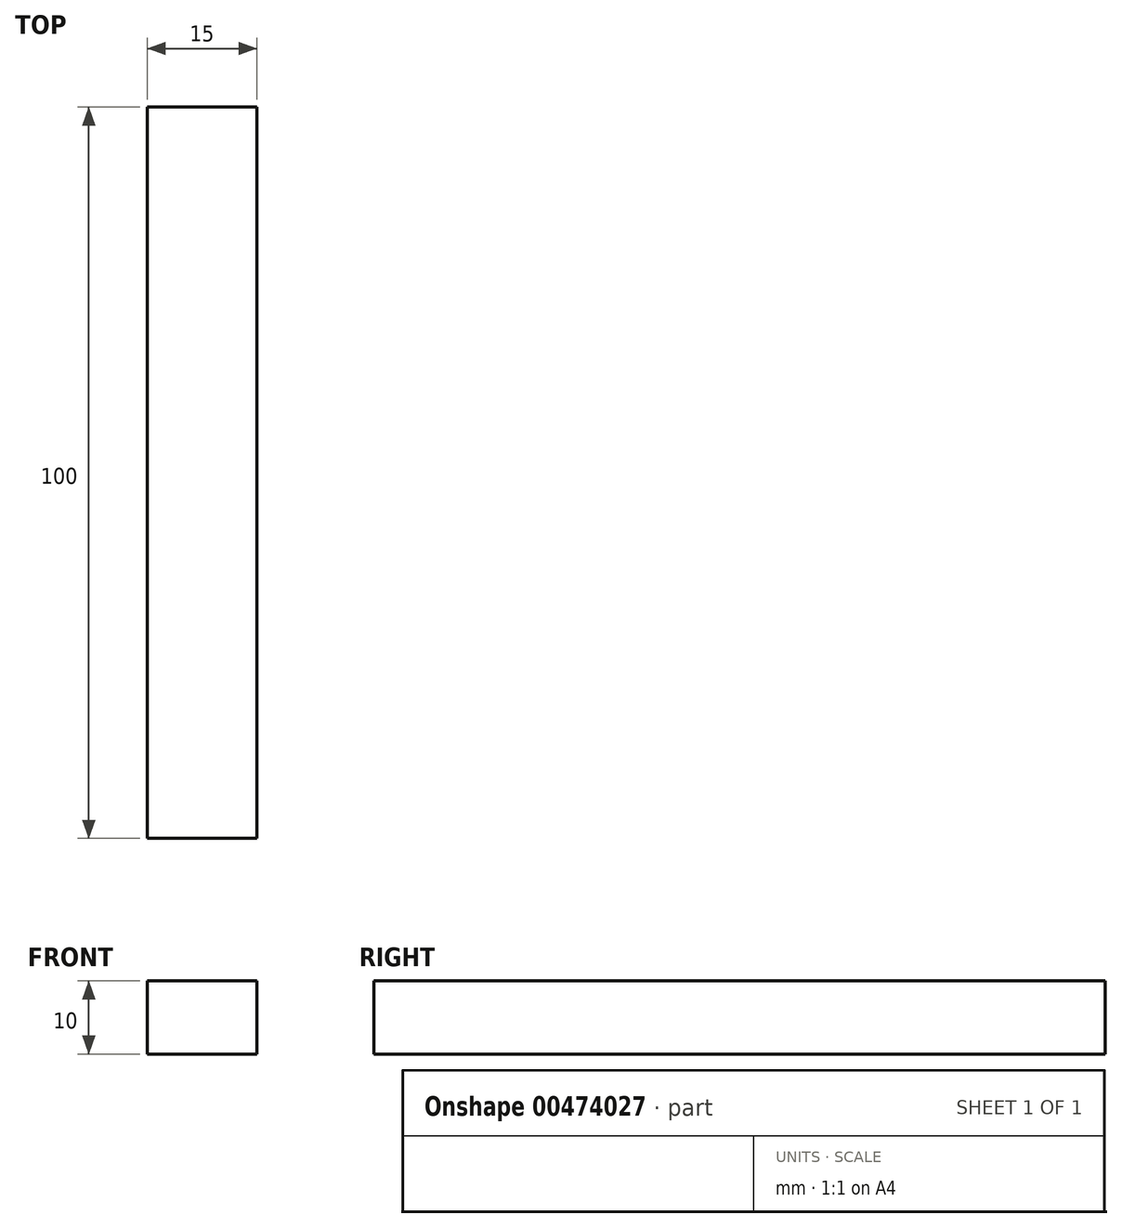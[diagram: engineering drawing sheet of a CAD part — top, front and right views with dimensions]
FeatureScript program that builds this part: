
annotation { "Feature Type Name" : "Feature", "Feature Type Description" : "" }
export const myFeature = defineFeature(function(context is Context, id is Id, definition is map)
    precondition{}
    {
        {
            var Q0;
            Q0=qCreatedBy(makeId("Front.planeOp"),FACE);
            var sketch = newSketch(context, id + "F0", { "sketchPlane" : qUnion([Q0])});
            skLineSegment(sketch, "E0.bottom", {"start": v(0, 0) * mm, "end": v(15, 0) * mm});
            skLineSegment(sketch, "E0.top", {"start": v(0, 10) * mm, "end": v(15, 10) * mm});
            skLineSegment(sketch, "E0.left", {"start": v(0, 0) * mm, "end": v(0, 10) * mm});
            skLineSegment(sketch, "E0.right", {"start": v(15, 0) * mm, "end": v(15, 10) * mm});
            skSolve(sketch);
        }
        {
            var Q0;
            Q0=qSketchRegion(id+"F0",true);
            extrude(context, id + "F1", {"entities" : qUnion([Q0]), "depth" : 100 * mm});
        }
    });
